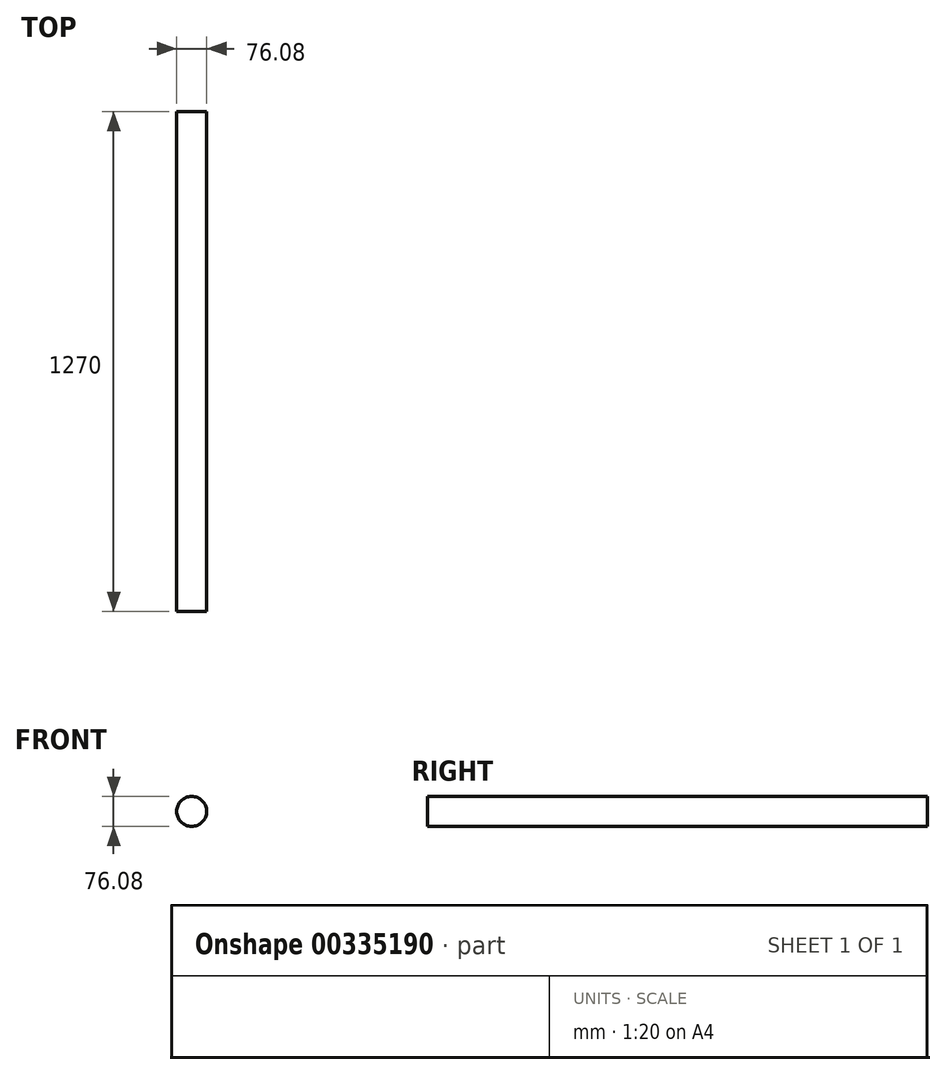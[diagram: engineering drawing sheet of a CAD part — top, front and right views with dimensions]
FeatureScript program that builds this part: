
annotation { "Feature Type Name" : "Feature", "Feature Type Description" : "" }
export const myFeature = defineFeature(function(context is Context, id is Id, definition is map)
    precondition{}
    {
        {
            var Q0;
            Q0=qCreatedBy(makeId("Front.planeOp"),FACE);
            var sketch = newSketch(context, id + "F0", { "sketchPlane" : qUnion([Q0])});
            skCircle(sketch, "E0", {"center": v(0, 0) * mm, "radius": 38.04 * mm});
            skSolve(sketch);
        }
        {
            var Q0;
            Q0=makeQuery(id+"F0.imprint","IMPRINT",FACE,{"disambiguationData":[TD([[makeQuery(id+"F0.imprint","IMPRINT",EDGE,{"derivedFrom":sQuery(id+"F0.wireOp",EDGE,"E0")}),1.0]])]});
            extrude(context, id + "F1", {"entities" : qUnion([Q0]), "depth" : 1270 * mm});
        }
    });
